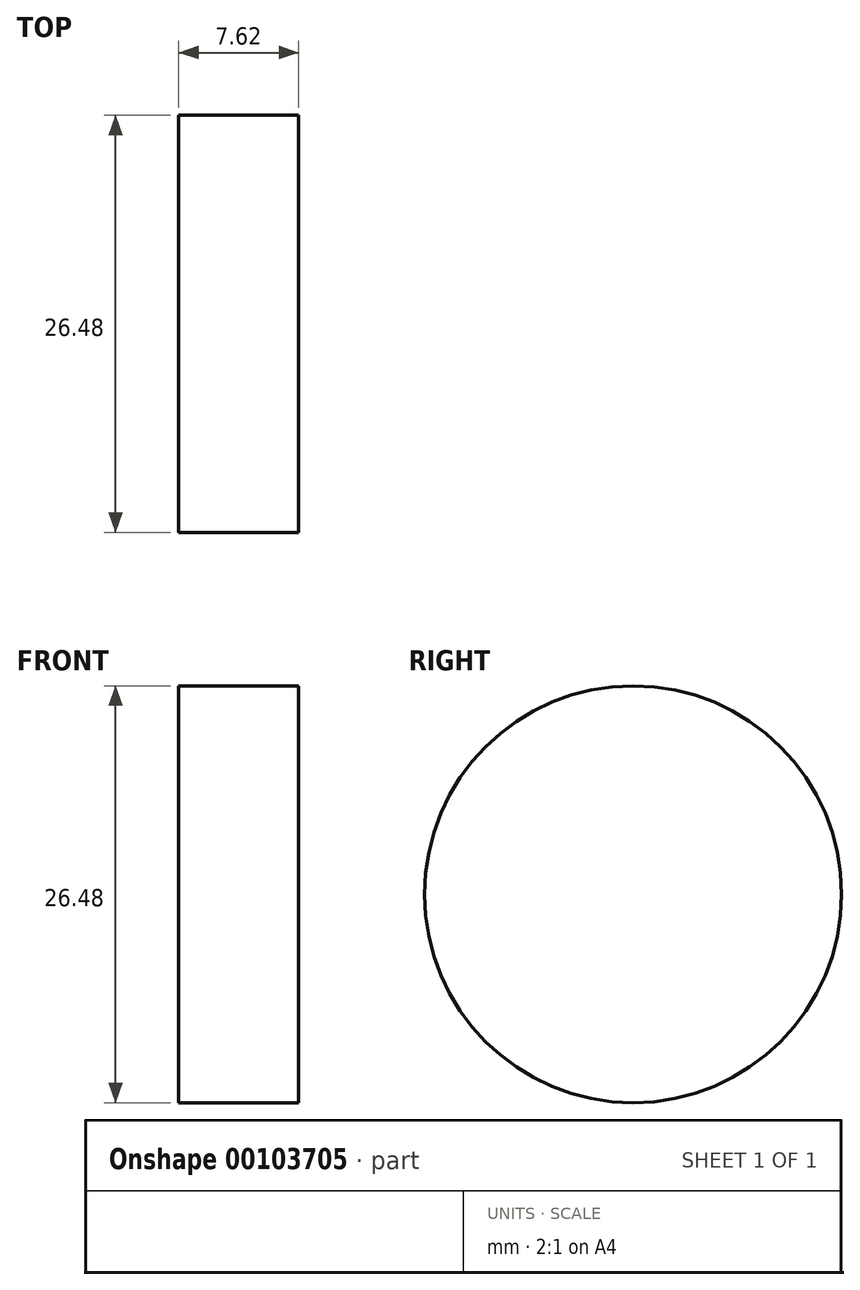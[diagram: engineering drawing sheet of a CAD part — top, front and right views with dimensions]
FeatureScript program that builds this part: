
annotation { "Feature Type Name" : "Feature", "Feature Type Description" : "" }
export const myFeature = defineFeature(function(context is Context, id is Id, definition is map)
    precondition{}
    {
        {
            var Q0;
            Q0=qCreatedBy(makeId("Right.planeOp"),FACE);
            var sketch = newSketch(context, id + "F0", { "sketchPlane" : qUnion([Q0])});
            skCircle(sketch, "E0", {"center": v(0, 0) * mm, "radius": 13.24 * mm});
            skSolve(sketch);
        }
        {
            var Q0;
            Q0 = qSketchRegion(id + "F0", true);
            extrude(context, id + "F1", {"entities" : qUnion([Q0]), "depth" : 7.62 * mm});
        }
    });
